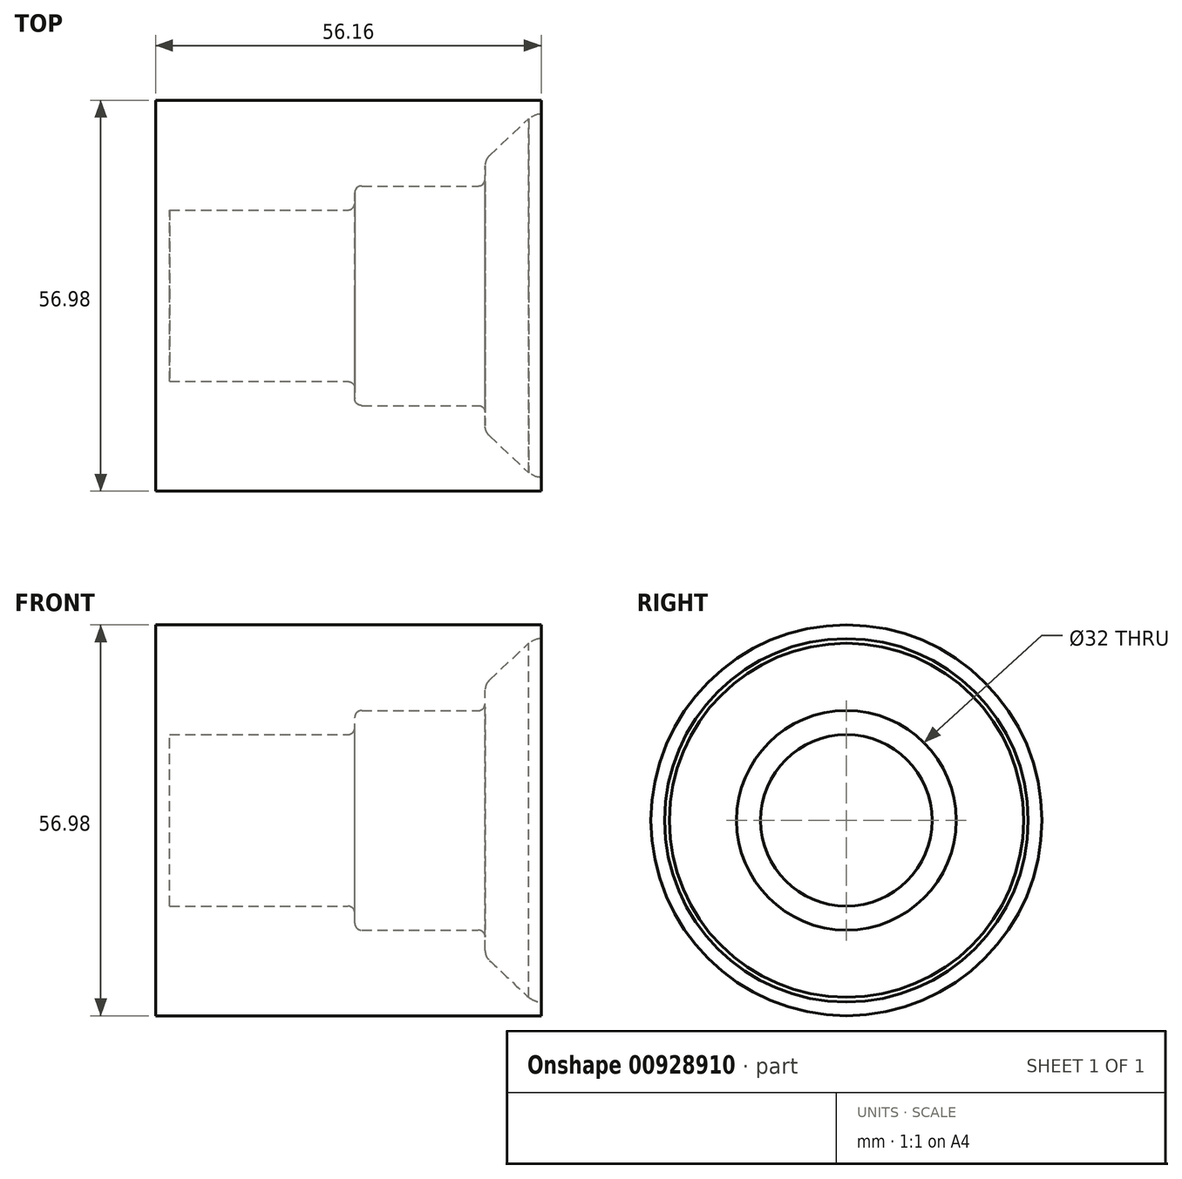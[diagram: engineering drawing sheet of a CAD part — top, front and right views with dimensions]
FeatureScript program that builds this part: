
annotation { "Feature Type Name" : "Feature", "Feature Type Description" : "" }
export const myFeature = defineFeature(function(context is Context, id is Id, definition is map)
    precondition{}
    {
        {
            var Q0;
            Q0=qCreatedBy(makeId("Front.planeOp"),FACE);
            var sketch = newSketch(context, id + "F0", { "sketchPlane" : qUnion([Q0])});
            skFitSpline(sketch, "E0", {"points": [v(51.84, 25.48) * mm, v(53.4, 26.36) * mm, v(54.9, 26.46) * mm, v(56.5, 25.94) * mm, v(57.63, 25.07) * mm, v(57.87, 24.79) * mm], "startDerivative": vector(6.57, 4.44) * mm, "endDerivative": vector(1.73, -2.25) * mm});
            skLineSegment(sketch, "E1", {"start": v(46.63, 20.43) * mm, "end": v(52.36, 25.83) * mm});
            skPoint(sketch, "E2.visualSharp", {"position": v(46, 19.84) * mm});
            skArc(sketch, "E2.filletArc", {"start": v(46.63, 20.43) * mm, "mid": v(46.16, 19.77) * mm, "end": v(46, 18.97) * mm});
            skLineSegment(sketch, "E3", {"start": v(45, 16) * mm, "end": v(28, 16) * mm});
            skLineSegment(sketch, "E4", {"start": v(27, 15) * mm, "end": v(27, 13.5) * mm});
            skLineSegment(sketch, "E5", {"start": v(26, 12.5) * mm, "end": v(0, 12.5) * mm});
            skLineSegment(sketch, "E6", {"start": v(0, 12.5) * mm, "end": v(0, 0) * mm});
            skLineSegment(sketch, "E7", {"start": v(46, 17) * mm, "end": v(46, 18.97) * mm});
            skPoint(sketch, "E8.visualSharp", {"position": v(27, 12.5) * mm});
            skArc(sketch, "E8.filletArc", {"start": v(26, 12.5) * mm, "mid": v(26.7, 12.8) * mm, "end": v(27, 13.5) * mm});
            skPoint(sketch, "E9.visualSharp", {"position": v(46, 16) * mm});
            skArc(sketch, "E9.filletArc", {"start": v(45, 16) * mm, "mid": v(45.7, 16.3) * mm, "end": v(46, 17) * mm});
            skLineSegment(sketch, "E10", {"start": v(39, 0) * mm, "end": v(0, 0) * mm});
            skPoint(sketch, "E11.visualSharp", {"position": v(27, 16) * mm});
            skArc(sketch, "E11.filletArc", {"start": v(28, 16) * mm, "mid": v(27.3, 15.7) * mm, "end": v(27, 15) * mm});
            skLineSegment(sketch, "E12", {"start": v(54.16, 26.5) * mm, "end": v(54.16, 28.5) * mm});
            skLineSegment(sketch, "E13", {"start": v(54.16, 28.5) * mm, "end": v(0, 28.5) * mm});
            skLineSegment(sketch, "E14", {"start": v(0, 28.5) * mm, "end": v(-2, 28.5) * mm});
            skLineSegment(sketch, "E15", {"start": v(-2, 28.5) * mm, "end": v(-2, 0) * mm});
            skLineSegment(sketch, "E16", {"start": v(-2, 0) * mm, "end": v(0, 0) * mm});
            skSolve(sketch);
        }
        {
            var Q0;
            {var subQ0=sQuery(id+"F0.wireOp",EDGE,"E0");Q0=makeQuery(id+"F0.imprint","IMPRINT",FACE,{"disambiguationData":[TD([[makeQuery(id+"F0.imprint","IMPRINT",EDGE,{"derivedFrom":subQ0}),1.0]])]});}
            var Q1;
            Q1=sQuery(id+"F0.wireOp",EDGE,"E10");
            revolve(context, id + "F1", {"surfaceOperationType" : NewSurfaceOperationType.NEW, "entities" : qUnion([Q0]), "axis" : qUnion([Q1]), "revolveType" : RevolveType.FULL});
        }
    });
